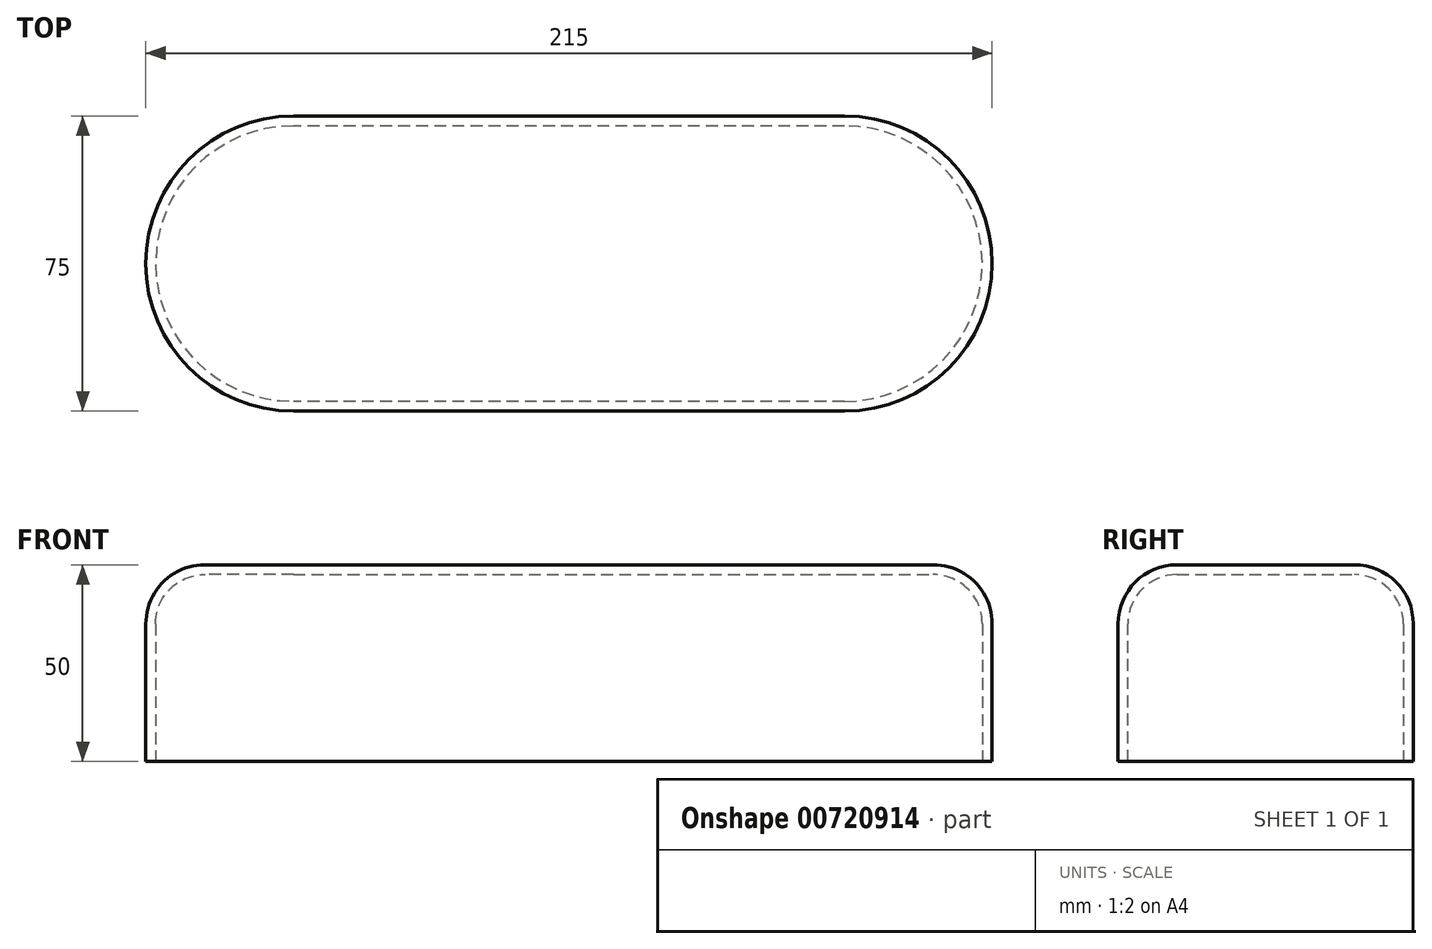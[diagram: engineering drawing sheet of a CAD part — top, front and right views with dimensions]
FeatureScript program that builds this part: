
annotation { "Feature Type Name" : "Feature", "Feature Type Description" : "" }
export const myFeature = defineFeature(function(context is Context, id is Id, definition is map)
    precondition{}
    {
        {
            var Q0;
            Q0=qCreatedBy(makeId("Top.planeOp"),FACE);
            var sketch = newSketch(context, id + "F0", { "sketchPlane" : qUnion([Q0])});
            skLineSegment(sketch, "E0", {"start": v(-63.75, 0) * mm, "end": v(76.25, 0) * mm});
            skLineSegment(sketch, "E1", {"start": v(0, 0) * mm, "end": v(0, -75) * mm});
            skLineSegment(sketch, "E2", {"start": v(-63.75, 0) * mm, "end": v(-63.75, -75) * mm});
            skLineSegment(sketch, "E3", {"start": v(-63.75, -75) * mm, "end": v(76.25, -75) * mm});
            skLineSegment(sketch, "E4", {"start": v(76.25, -75) * mm, "end": v(76.25, 0) * mm});
            skArc(sketch, "E5", {"start": v(-63.75, 0) * mm, "mid": v(-101.25, -37.5) * mm, "end": v(-63.75, -75) * mm});
            skArc(sketch, "E6", {"start": v(76.25, -75) * mm, "mid": v(113.75, -37.5) * mm, "end": v(76.25, 0) * mm});
            skSolve(sketch);
        }
        {
            var Q0;
            Q0=makeQuery(id+"F0.imprint","IMPRINT",FACE,{"disambiguationData":[TD([[makeQuery(id+"F0.imprint","IMPRINT",EDGE,{"derivedFrom":sQuery(id+"F0.wireOp",EDGE,"E2")}),-1.0]])]});
            var Q1;
            {var subQ3=sQuery(id+"F0.wireOp",EDGE,"E1");Q1=makeQuery(id+"F0.imprint","IMPRINT",FACE,{"disambiguationData":[TD([[makeQuery(id+"F0.imprint","IMPRINT",EDGE,{"derivedFrom":subQ3}),-1.0]])]});}
            var Q2;
            {var subQ3=sQuery(id+"F0.wireOp",EDGE,"E1");Q2=makeQuery(id+"F0.imprint","IMPRINT",FACE,{"disambiguationData":[TD([[makeQuery(id+"F0.imprint","IMPRINT",EDGE,{"derivedFrom":subQ3}),1.0]])]});}
            var Q3;
            Q3=makeQuery(id+"F0.imprint","IMPRINT",FACE,{"disambiguationData":[TD([[makeQuery(id+"F0.imprint","IMPRINT",EDGE,{"derivedFrom":sQuery(id+"F0.wireOp",EDGE,"E4")}),-1.0]])]});
            extrude(context, id + "F1", {"entities" : qUnion([Q0, Q1, Q2, Q3]), "depth" : 65 * mm, "offsetDistance" : 25 * mm});
        }
        {
            var Q0;
            Q0=makeQuery(id+"F1.opExtrude","CAP_EDGE",EDGE,{"disambiguationData":[OSD([sQuery(id+"F0.wireOp",EDGE,"E5")])],"isStart":false});
            var Q1;
            Q1=makeQuery(id+"F1.opExtrude","CAP_EDGE",EDGE,{"disambiguationData":[OSD([sQuery(id+"F0.wireOp",EDGE,"E6")])],"isStart":true});
            fillet(context, id + "F2", {"entities" : qUnion([Q0, Q1]), "radius" : 15 * mm, "tangentPropagation" : true, "allowEdgeOverflow" : false});
        }
        {
            var Q0;
            {var subQ0=sQuery(id+"F0.wireOp",EDGE,"E3");Q0=makeQuery(id+"F2.opFillet","BLEND_FACE",FACE,{"disambiguationData":[OSD([subQ0]),TDD([makeQuery(id+"F1.opExtrude","CAP_EDGE",EDGE,{"disambiguationData":[OSD([subQ0])],"isStart":true})])]});}
            var Q1;
            {var subQ0=sQuery(id+"F0.wireOp",EDGE,"E5");Q1=makeQuery(id+"F2.opFillet","BLEND_FACE",FACE,{"disambiguationData":[OSD([subQ0]),TDD([makeQuery(id+"F1.opExtrude","CAP_EDGE",EDGE,{"disambiguationData":[OSD([subQ0])],"isStart":true})])]});}
            var Q2;
            Q2=makeQuery(id+"F1.opExtrude","CAP_FACE",FACE,{"disambiguationData":[OSD([sQuery(id+"F0.wireOp",EDGE,"E0"),sQuery(id+"F0.wireOp",EDGE,"E3"),sQuery(id+"F0.wireOp",EDGE,"E5"),sQuery(id+"F0.wireOp",EDGE,"E6")])],"isStart":true});
            var Q3;
            {var subQ0=sQuery(id+"F0.wireOp",EDGE,"E6");Q3=makeQuery(id+"F2.opFillet","BLEND_FACE",FACE,{"disambiguationData":[OSD([subQ0]),TDD([makeQuery(id+"F1.opExtrude","CAP_EDGE",EDGE,{"disambiguationData":[OSD([subQ0])],"isStart":true})])]});}
            var Q4;
            {var subQ0=sQuery(id+"F0.wireOp",EDGE,"E0");Q4=makeQuery(id+"F2.opFillet","BLEND_FACE",FACE,{"disambiguationData":[OSD([subQ0]),TDD([makeQuery(id+"F1.opExtrude","CAP_EDGE",EDGE,{"disambiguationData":[OSD([subQ0])],"isStart":true})])]});}
            shell(context, id + "F3", {"entities" : qUnion([Q0, Q1, Q2, Q3, Q4]), "thickness" : 2.5 * mm});
        }
    });
